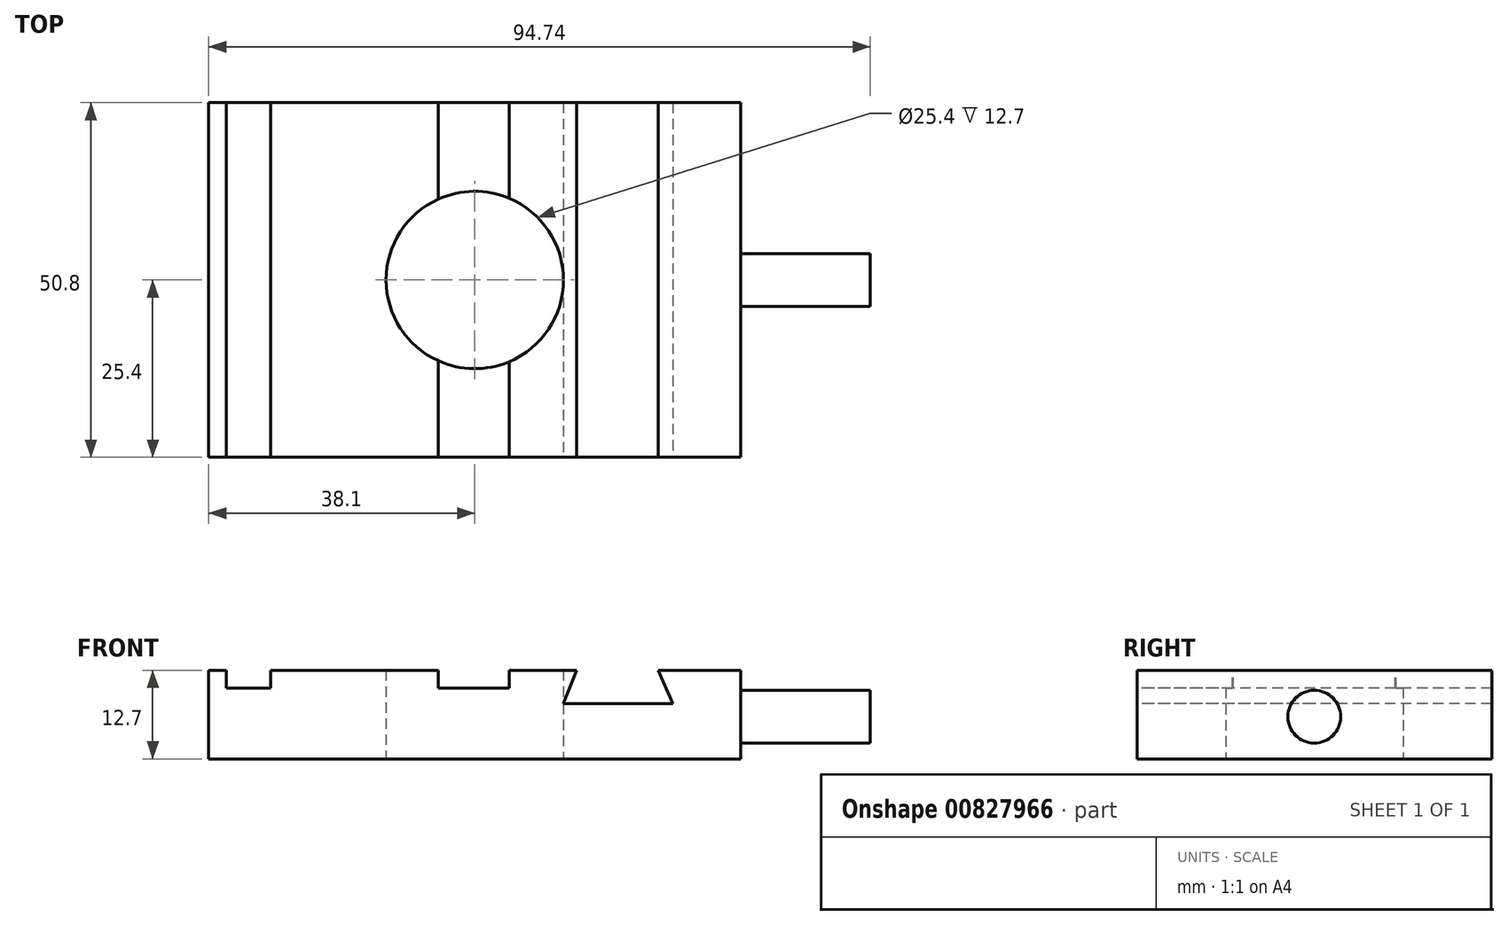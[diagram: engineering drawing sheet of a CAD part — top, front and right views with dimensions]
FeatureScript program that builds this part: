
annotation { "Feature Type Name" : "Feature", "Feature Type Description" : "" }
export const myFeature = defineFeature(function(context is Context, id is Id, definition is map)
    precondition{}
    {
        {
            var Q0;
            Q0=qCreatedBy(makeId("Top.planeOp"),FACE);
            var sketch = newSketch(context, id + "F0", { "sketchPlane" : qUnion([Q0])});
            skLineSegment(sketch, "E0.bottom", {"start": v(-38.1, 25.4) * mm, "end": v(38.1, 25.4) * mm});
            skLineSegment(sketch, "E0.top", {"start": v(-38.1, -25.4) * mm, "end": v(38.1, -25.4) * mm});
            skLineSegment(sketch, "E0.left", {"start": v(-38.1, 25.4) * mm, "end": v(-38.1, -25.4) * mm});
            skLineSegment(sketch, "E0.right", {"start": v(38.1, 25.4) * mm, "end": v(38.1, -25.4) * mm});
            skPoint(sketch, "E0.middle", {"position": v(0, 0) * mm});
            skCircle(sketch, "E1", {"center": v(0, 0) * mm, "radius": 12.7 * mm});
            skSolve(sketch);
        }
        {
            var Q0;
            Q0 = qSketchRegion(id + "F0", true);
            extrude(context, id + "F1", {"entities" : qUnion([Q0]), "depth" : 12.7 * mm, "offsetDistance" : 25.4 * mm});
        }
        {
            var Q0;
            Q0=makeQuery(id+"F1.opExtrude","CAP_FACE",FACE,{"disambiguationData":[OSD([sQuery(id+"F0.wireOp",EDGE,"E0.bottom"),sQuery(id+"F0.wireOp",EDGE,"E0.top"),sQuery(id+"F0.wireOp",EDGE,"E0.left"),sQuery(id+"F0.wireOp",EDGE,"E0.right"),sQuery(id+"F0.wireOp",EDGE,"E1")])],"isStart":false});
            var sketch = newSketch(context, id + "F2", { "sketchPlane" : qUnion([Q0])});
            skLineSegment(sketch, "E2.bottom", {"start": v(-35.56, 25.4) * mm, "end": v(-29.21, 25.4) * mm});
            skLineSegment(sketch, "E2.top", {"start": v(-35.56, -25.4) * mm, "end": v(-29.21, -25.4) * mm});
            skLineSegment(sketch, "E2.left", {"start": v(-35.56, 25.4) * mm, "end": v(-35.56, -25.4) * mm});
            skLineSegment(sketch, "E2.right", {"start": v(-29.21, 25.4) * mm, "end": v(-29.21, -25.4) * mm});
            skLineSegment(sketch, "E3", {"start": v(-5.25, 25.4) * mm, "end": v(-5.25, -25.4) * mm});
            skLineSegment(sketch, "E4", {"start": v(4.9, 25.4) * mm, "end": v(4.9, -25.4) * mm});
            skLineSegment(sketch, "E5", {"start": v(0, 25.4) * mm, "end": v(0, -25.4) * mm});
            skSolve(sketch);
        }
        {
            var Q0;
            Q0 = qSketchRegion(id + "F2", true);
            var Q1;
            {var subQ0=sQuery(id+"F2.wireOp",EDGE,"E3");var subQ1=makeQuery(id+"F1.opExtrude","CAP_EDGE",EDGE,{"disambiguationData":[OSD([sQuery(id+"F0.wireOp",EDGE,"E0.top")])],"isStart":false});var subQ2=makeQuery(id+"F2.imprint","INTERSECT",VERTEX,{"derivedFrom":[subQ1,subQ0]});Q1=makeQuery(id+"F2.imprint","IMPRINT",FACE,{"disambiguationData":[TD([[makeQuery(id+"F2.imprint","IMPRINT",EDGE,{"disambiguationData":[TD([[subQ2,1.0]])],"derivedFrom":subQ0}),1.0]])]});}
            var Q2;
            {var subQ0=sQuery(id+"F2.wireOp",EDGE,"E4");var subQ1=makeQuery(id+"F1.opExtrude","CAP_EDGE",EDGE,{"disambiguationData":[OSD([sQuery(id+"F0.wireOp",EDGE,"E0.top")])],"isStart":false});var subQ2=makeQuery(id+"F2.imprint","INTERSECT",VERTEX,{"derivedFrom":[subQ1,subQ0]});Q2=makeQuery(id+"F2.imprint","IMPRINT",FACE,{"disambiguationData":[TD([[makeQuery(id+"F2.imprint","IMPRINT",EDGE,{"disambiguationData":[TD([[subQ2,1.0]])],"derivedFrom":subQ0}),-1.0]])]});}
            var Q3;
            {var subQ0=sQuery(id+"F2.wireOp",EDGE,"E3");var subQ1=makeQuery(id+"F1.opExtrude","CAP_EDGE",EDGE,{"disambiguationData":[OSD([sQuery(id+"F0.wireOp",EDGE,"E0.bottom")])],"isStart":false});var subQ2=makeQuery(id+"F2.imprint","INTERSECT",VERTEX,{"derivedFrom":[subQ1,subQ0]});Q3=makeQuery(id+"F2.imprint","IMPRINT",FACE,{"disambiguationData":[TD([[makeQuery(id+"F2.imprint","IMPRINT",EDGE,{"disambiguationData":[TD([[subQ2,-1.0]])],"derivedFrom":subQ0}),1.0]])]});}
            var Q4;
            {var subQ0=sQuery(id+"F2.wireOp",EDGE,"E4");var subQ1=makeQuery(id+"F1.opExtrude","CAP_EDGE",EDGE,{"disambiguationData":[OSD([sQuery(id+"F0.wireOp",EDGE,"E0.bottom")])],"isStart":false});var subQ2=makeQuery(id+"F2.imprint","INTERSECT",VERTEX,{"derivedFrom":[subQ1,subQ0]});Q4=makeQuery(id+"F2.imprint","IMPRINT",FACE,{"disambiguationData":[TD([[makeQuery(id+"F2.imprint","IMPRINT",EDGE,{"disambiguationData":[TD([[subQ2,-1.0]])],"derivedFrom":subQ0}),-1.0]])]});}
            extrude(context, id + "F3", {"entities" : qUnion([Q0, Q1, Q2, Q3, Q4]), "operationType" : NewBodyOperationType.REMOVE, "oppositeDirection" : true, "depth" : 2.54 * mm, "offsetDistance" : 25.4 * mm});
        }
        {
            var Q0;
            Q0=makeQuery(id+"F1.opExtrude","SWEPT_FACE",FACE,{"disambiguationData":[OSD([sQuery(id+"F0.wireOp",EDGE,"E0.right")])]});
            var sketch = newSketch(context, id + "F4", { "sketchPlane" : qUnion([Q0])});
            skCircle(sketch, "E6", {"center": v(0, 6.04) * mm, "radius": 3.78 * mm});
            skSolve(sketch);
        }
        {
            var Q0;
            Q0 = qSketchRegion(id + "F4", true);
            extrude(context, id + "F5", {"entities" : qUnion([Q0]), "operationType" : NewBodyOperationType.ADD, "depth" : 18.54 * mm, "offsetDistance" : 25.4 * mm});
        }
        {
            var Q0;
            Q0=makeQuery(id+"F1.opExtrude","SWEPT_FACE",FACE,{"disambiguationData":[OSD([sQuery(id+"F0.wireOp",EDGE,"E0.top")])]});
            var sketch = newSketch(context, id + "F6", { "sketchPlane" : qUnion([Q0])});
            skLineSegment(sketch, "E7", {"start": v(14.6, 12.7) * mm, "end": v(26.26, 12.7) * mm});
            skLineSegment(sketch, "E8", {"start": v(26.26, 12.7) * mm, "end": v(28.36, 7.92) * mm});
            skLineSegment(sketch, "E9", {"start": v(28.36, 7.92) * mm, "end": v(12.7, 7.92) * mm});
            skLineSegment(sketch, "E10", {"start": v(12.7, 7.92) * mm, "end": v(14.6, 12.7) * mm});
            skSolve(sketch);
        }
        {
            var Q0;
            Q0 = qSketchRegion(id + "F6", true);
            extrude(context, id + "F7", {"entities" : qUnion([Q0]), "operationType" : NewBodyOperationType.REMOVE, "endBound" : BoundingType.THROUGH_ALL, "oppositeDirection" : true, "depth" : 53.1 * mm, "offsetDistance" : 25.4 * mm});
        }
    });
